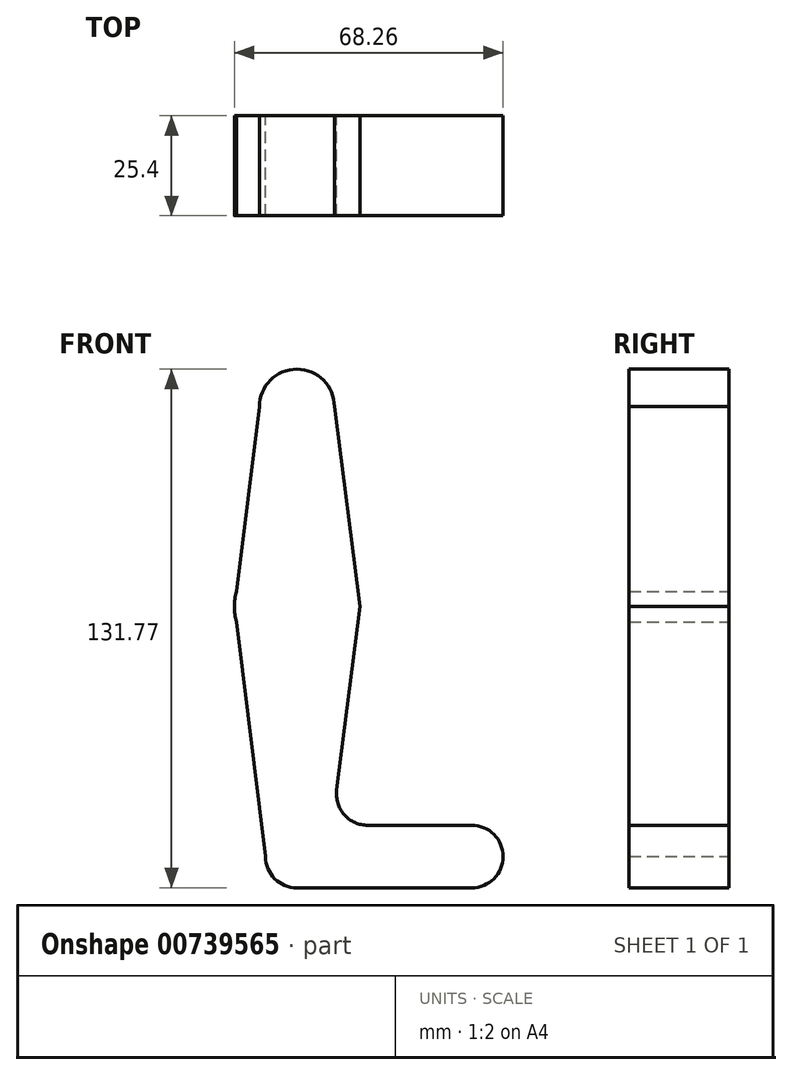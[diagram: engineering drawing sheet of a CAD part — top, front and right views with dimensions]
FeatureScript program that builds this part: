
annotation { "Feature Type Name" : "Feature", "Feature Type Description" : "" }
export const myFeature = defineFeature(function(context is Context, id is Id, definition is map)
    precondition{}
    {
        {
            var Q0;
            Q0=qCreatedBy(makeId("Front.planeOp"),FACE);
            var sketch = newSketch(context, id + "F0", { "sketchPlane" : qUnion([Q0])});
            skLineSegment(sketch, "E0", {"start": v(0, 0) * mm, "end": v(0, 114.3) * mm, "construction": true});
            skLineSegment(sketch, "E1", {"start": v(0, 0) * mm, "end": v(44.45, 0) * mm, "construction": true});
            skCircle(sketch, "E2", {"center": v(44.45, 0) * mm, "radius": 7.94 * mm});
            skCircle(sketch, "E3", {"center": v(0, 0) * mm, "radius": 7.94 * mm});
            skCircle(sketch, "E4", {"center": v(0, 114.3) * mm, "radius": 9.53 * mm});
            skCircle(sketch, "E5", {"center": v(0, 63.5) * mm, "radius": 15.87 * mm});
            skLineSegment(sketch, "E6", {"start": v(-9.53, 114.3) * mm, "end": v(-15.87, 63.5) * mm});
            skLineSegment(sketch, "E7", {"start": v(-15.87, 63.5) * mm, "end": v(-7.94, 0) * mm});
            skLineSegment(sketch, "E8", {"start": v(9.53, 114.3) * mm, "end": v(16, 63.5) * mm});
            skLineSegment(sketch, "E9", {"start": v(16, 63.5) * mm, "end": v(10.13, 16.88) * mm});
            skLineSegment(sketch, "E10", {"start": v(18.02, 7.94) * mm, "end": v(44.45, 7.94) * mm});
            skLineSegment(sketch, "E11", {"start": v(44.45, -7.94) * mm, "end": v(0, -7.94) * mm});
            skPoint(sketch, "E12.newPointB", {"position": v(0, 7.94) * mm});
            skArc(sketch, "E12.filletArc", {"start": v(10.13, 16.88) * mm, "mid": v(12.05, 10.63) * mm, "end": v(18.02, 7.94) * mm});
            skCircle(sketch, "E13", {"center": v(0, 114.3) * mm, "radius": 3.18 * mm});
            skCircle(sketch, "E14", {"center": v(0, 63.5) * mm, "radius": 3.18 * mm});
            skCircle(sketch, "E15", {"center": v(0, 0) * mm, "radius": 3.18 * mm});
            skCircle(sketch, "E16", {"center": v(44.45, 0) * mm, "radius": 3.18 * mm});
            skSolve(sketch);
        }
        {
            var Q0;
            Q0=makeQuery(id+"F0.imprint","IMPRINT",FACE,{"disambiguationData":[TD([[makeQuery(id+"F0.imprint","IMPRINT",EDGE,{"derivedFrom":sQuery(id+"F0.wireOp",EDGE,"E16")}),-1.0]])]});
            var Q1;
            Q1=makeQuery(id+"F0.imprint","IMPRINT",FACE,{"disambiguationData":[TD([[makeQuery(id+"F0.imprint","IMPRINT",EDGE,{"derivedFrom":sQuery(id+"F0.wireOp",EDGE,"E14")}),-1.0]])]});
            var Q2;
            {var subQ10=sQuery(id+"F0.wireOp",EDGE,"E9");Q2=makeQuery(id+"F0.imprint","IMPRINT",FACE,{"disambiguationData":[TD([[makeQuery(id+"F0.imprint","IMPRINT",EDGE,{"derivedFrom":subQ10}),-1.0]])]});}
            var Q3;
            {var subQ0=sQuery(id+"F0.wireOp",EDGE,"E6");var subQ1=sQuery(id+"F0.wireOp",EDGE,"E4");var subQ2=makeQuery(id+"F0.imprint","INTERSECT",VERTEX,{"derivedFrom":[subQ1,subQ0]});Q3=makeQuery(id+"F0.imprint","IMPRINT",FACE,{"disambiguationData":[TD([[makeQuery(id+"F0.imprint","IMPRINT",EDGE,{"disambiguationData":[TD([[subQ2,-1.0]])],"derivedFrom":subQ1}),-1.0]])]});}
            var Q4;
            Q4=makeQuery(id+"F0.imprint","IMPRINT",FACE,{"disambiguationData":[TD([[makeQuery(id+"F0.imprint","IMPRINT",EDGE,{"derivedFrom":sQuery(id+"F0.wireOp",EDGE,"E13")}),-1.0]])]});
            var Q5;
            Q5=makeQuery(id+"F0.imprint","IMPRINT",FACE,{"disambiguationData":[TD([[makeQuery(id+"F0.imprint","IMPRINT",EDGE,{"derivedFrom":sQuery(id+"F0.wireOp",EDGE,"E16")}),1.0]])]});
            var Q6;
            Q6=makeQuery(id+"F0.imprint","IMPRINT",FACE,{"disambiguationData":[TD([[makeQuery(id+"F0.imprint","IMPRINT",EDGE,{"derivedFrom":sQuery(id+"F0.wireOp",EDGE,"E15")}),1.0]])]});
            var Q7;
            Q7=makeQuery(id+"F0.imprint","IMPRINT",FACE,{"disambiguationData":[TD([[makeQuery(id+"F0.imprint","IMPRINT",EDGE,{"derivedFrom":sQuery(id+"F0.wireOp",EDGE,"E14")}),1.0]])]});
            var Q8;
            Q8=makeQuery(id+"F0.imprint","IMPRINT",FACE,{"disambiguationData":[TD([[makeQuery(id+"F0.imprint","IMPRINT",EDGE,{"derivedFrom":sQuery(id+"F0.wireOp",EDGE,"E13")}),1.0]])]});
            var Q9;
            {var subQ0=sQuery(id+"F0.wireOp",EDGE,"E7");var subQ1=sQuery(id+"F0.wireOp",EDGE,"E5");var subQ3=makeQuery(id+"F0.imprint","INTERSECT",VERTEX,{"derivedFrom":[subQ1,subQ0]});Q9=makeQuery(id+"F0.imprint","IMPRINT",FACE,{"disambiguationData":[TD([[makeQuery(id+"F0.imprint","IMPRINT",EDGE,{"disambiguationData":[TD([[subQ3,1.0]])],"derivedFrom":subQ1}),1.0]])]});}
            var Q10;
            {var subQ0=sQuery(id+"F0.wireOp",EDGE,"E6");var subQ1=sQuery(id+"F0.wireOp",EDGE,"E5");var subQ3=makeQuery(id+"F0.imprint","INTERSECT",VERTEX,{"derivedFrom":[subQ1,subQ0]});Q10=makeQuery(id+"F0.imprint","IMPRINT",FACE,{"disambiguationData":[TD([[makeQuery(id+"F0.imprint","IMPRINT",EDGE,{"disambiguationData":[TD([[subQ3,-1.0]])],"derivedFrom":subQ1}),1.0]])]});}
            var Q11;
            Q11=makeQuery(id+"F0.imprint","IMPRINT",FACE,{"disambiguationData":[TD([[makeQuery(id+"F0.imprint","IMPRINT",EDGE,{"derivedFrom":sQuery(id+"F0.wireOp",EDGE,"E15")}),-1.0]])]});
            var Q12;
            Q12=sQuery(id+"F0.wireOp",EDGE,"E12.filletArc");
            var Q13;
            Q13=sQuery(id+"F0.wireOp",EDGE,"E11");
            var Q14;
            Q14=sQuery(id+"F0.wireOp",EDGE,"E10");
            var Q15;
            Q15=sQuery(id+"F0.wireOp",EDGE,"E9");
            var Q16;
            Q16=sQuery(id+"F0.wireOp",EDGE,"E8");
            var Q17;
            Q17=sQuery(id+"F0.wireOp",EDGE,"E7");
            var Q18;
            Q18=sQuery(id+"F0.wireOp",EDGE,"E6");
            var Q19;
            Q19=sQuery(id+"F0.wireOp",EDGE,"E5");
            var Q20;
            Q20=sQuery(id+"F0.wireOp",EDGE,"E4");
            var Q21;
            Q21=sQuery(id+"F0.wireOp",EDGE,"E3");
            var Q22;
            Q22=sQuery(id+"F0.wireOp",EDGE,"E2");
            var Q23;
            Q23=sQuery(id+"F0.wireOp",EDGE,"E15");
            var Q24;
            Q24=sQuery(id+"F0.wireOp",EDGE,"E14");
            var Q25;
            Q25=sQuery(id+"F0.wireOp",EDGE,"E16");
            var Q26;
            Q26=sQuery(id+"F0.wireOp",EDGE,"E13");
            extrude(context, id + "F1", {"entities" : qUnion([Q0, Q1, Q2, Q3, Q4, Q5, Q6, Q7, Q8, Q9, Q10, Q11]), "surfaceEntities" : qUnion([Q12, Q13, Q14, Q15, Q16, Q17, Q18, Q19, Q20, Q21, Q22, Q23, Q24, Q25, Q26]), "depth" : 25.4 * mm, "offsetDistance" : 25.4 * mm});
        }
    });
